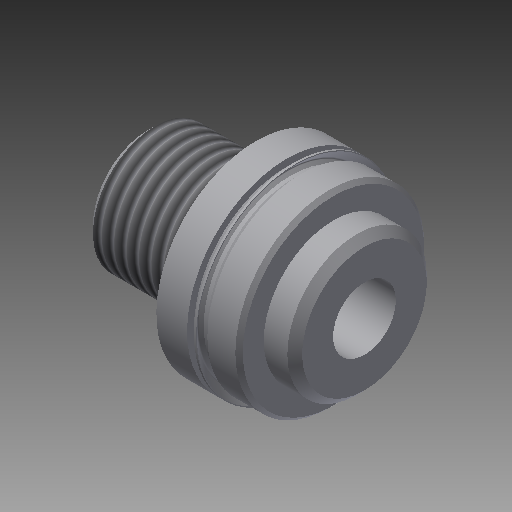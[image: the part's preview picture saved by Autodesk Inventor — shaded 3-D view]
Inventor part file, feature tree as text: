
AUTODESK INVENTOR PART (.ipt)
format: ipt  version: 2018.3 (Build 223284000, 284)  size: 261,120 bytes
history: native  units: in
note: dims shown in document units (in); Inventor stores cm internally (conversion verified against a paired STEP export)
features: other x84, sketch x5, revolve x4, thread x1, hole x1
ambient origin geometry x8: Origin, YZ Plane, XZ Plane, XY Plane, X Axis, Y Axis, Z Axis, Center Point
bodies: Solid1 (feature_tree)
feature tree (95):
  revolve  "Revolution1"  [1 undecoded]
  thread  "Thread1"  [1 undecoded]
  revolve  "Revolution2"  Angle=360.0deg
  revolve  "Revolution3"  [1 undecoded]
  hole  "Hole1"  [1 undecoded]
  revolve  "Revolution4"  [1 undecoded]
  other  "hh_XY"
  other  "hh_YZ"
  other  "hh_ZX"
  other  "hh_X"
  other  "hh_Y"
  other  "hh_Z"
  other  "hh_Center"
  other  "rod_guide_XY"
  other  "rod_guide_YZ"
  other  "rod_guide_ZX"
  other  "rod_guide_X"
  other  "rod_guide_Y"
  other  "rod_guide_Z"
  other  "rod_guide_Center"
  other  "t1_XY"
  other  "t1_YZ"
  other  "t1_ZX"
  other  "t1_X"
  other  "t1_Y"
  other  "t1_Z"
  other  "t1_Center"
  other  "t111_XY"
  other  "t111_YZ"
  other  "t111_ZX"
  other  "t111_X"
  other  "t111_Y"
  other  "t111_Z"
  other  "t111_Center"
  other  "to_foot_bracket_XY"
  other  "to_foot_bracket_YZ"
  other  "to_foot_bracket_ZX"
  other  "to_foot_bracket_X"
  other  "to_foot_bracket_Y"
  other  "to_foot_bracket_Z"
  other  "to_foot_bracket_Center"
  other  "to_nut_XY"
  other  "to_nut_YZ"
  other  "to_nut_ZX"
  other  "to_nut_X"
  other  "to_nut_Y"
  other  "to_nut_Z"
  other  "to_nut_Center"
  other  "to_rod_XY"
  other  "to_rod_YZ"
  other  "to_rod_ZX"
  other  "to_rod_X"
  other  "to_rod_Y"
  other  "to_rod_Z"
  other  "to_rod_Center"
  other  "to_screw_XY"
  other  "to_screw_YZ"
  other  "to_screw_ZX"
  other  "to_screw_X"
  other  "to_screw_Y"
  other  "to_screw_Z"
  other  "to_screw_Center"
  other  "to_trunnion_brackets_XY"
  other  "to_trunnion_brackets_YZ"
  other  "to_trunnion_brackets_ZX"
  other  "to_trunnion_brackets_X"
  other  "to_trunnion_brackets_Y"
  other  "to_trunnion_brackets_Z"
  other  "to_trunnion_brackets_Center"
  other  "to_trunnion_brackets1_XY"
  other  "to_trunnion_brackets1_YZ"
  other  "to_trunnion_brackets1_ZX"
  other  "to_trunnion_brackets1_X"
  other  "to_trunnion_brackets1_Y"
  other  "to_trunnion_brackets1_Z"
  other  "to_trunnion_brackets1_Center"
  other  "to_trunnion_brackets2_XY"
  other  "to_trunnion_brackets2_YZ"
  other  "to_trunnion_brackets2_ZX"
  other  "to_trunnion_brackets2_X"
  other  "to_trunnion_brackets2_Y"
  other  "to_trunnion_brackets2_Z"
  other  "to_trunnion_brackets2_Center"
  other  "to_tube_XY"
  other  "to_tube_YZ"
  other  "to_tube_ZX"
  other  "to_tube_X"
  other  "to_tube_Y"
  other  "to_tube_Z"
  other  "to_tube_Center"
  sketch  "Sketch_1"  dims[d0=360.0deg d1=0.4083in d2=0.0in d3=360.0deg]
  sketch  "Sketch_3"  dims[d4=360.0deg]
  sketch  "Sketch_4"  dims[d5=0.2535in d6=0.75in d7=0.2735in d8=0.25in d9=90.0deg d10=0.875in d11=0.0in d12=360.0deg]
  sketch  "Sketch4"  dims[d13=0.0in d14=0.0in d15=0.0in d16=0.0in d17=0.0in d18=0.0in]
  sketch  "Sketch_47"
note: 5 required parameter values undecoded (feature->parameter linkage not recoverable at this tier; creation-order binding heuristic only, values carry confidence <= 0.55)